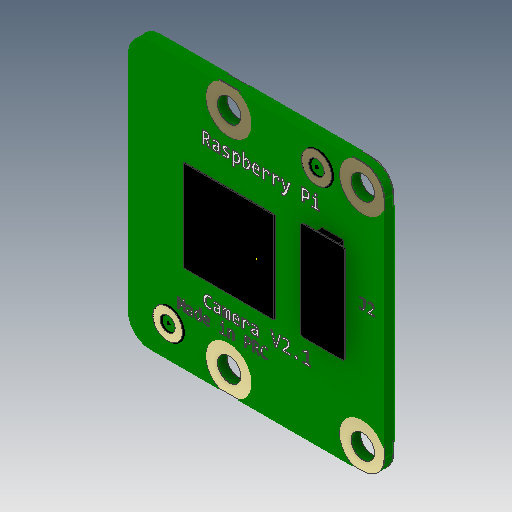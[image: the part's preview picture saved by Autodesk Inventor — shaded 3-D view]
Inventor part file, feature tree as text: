
AUTODESK INVENTOR PART (.ipt)
format: ipt  version: 2020 (Build 240168000, 168)  size: 2,342,912 bytes
history: native  units: mm
features: other x18, extrude x10, sketch x5, projected_geometry x5, hole x1, fillet x1
ambient origin geometry x8: Origin, YZ Plane, XZ Plane, XY Plane, X Axis, Y Axis, Z Axis, Center Point
bodies: Body1 (feature_tree), Body2 (feature_tree), Body3 (feature_tree), Body4 (feature_tree), Body5 (feature_tree), Body6 (feature_tree), Body7 (feature_tree), Body8 (feature_tree), Body9 (feature_tree)
feature tree (40):
  other  "PCB"
  sketch  "Boceto1"  dims[d0=23.862mm d1=25.0mm]
  extrude  "PCB_EXT"  Depth=25.0mm
  hole  "PADS_PCB_DRILL"  [1 undecoded]
  sketch  "Boceto2"  dims[d7=2.0mm d8=2.0mm]
  extrude  "PADS_PCB_DRILL_EXT"  Depth=1.0mm TaperAngle=0.0deg
  other  "FOTO"
  other  "SUPERIOR_PADS"
  extrude  "PADS_GOLDEN_UPPER_EXT"  Depth=2.2mm
  other  "INFERIOR_PADS"
  extrude  "PADS_GOLDEN_LOWER_EXT"  Depth=0.2mm
  extrude  "TEXTS_EXT"  Depth=0.2mm
  other  "REF_CON"
  extrude  "CONN"  Depth=0.2mm
  extrude  "CAM_BED"  Depth=0.2mm TaperAngle=0.0deg
  other  "PLANO_CON"
  extrude  "CONN_TOP"  Depth=0.2mm
  fillet  "Empalme2"  [1 undecoded]
  other  "REF_PADS_DRAW"
  extrude  "REF_PADS_DIAGONAL"  Depth=0.2mm TaperAngle=0.0deg
  extrude  "REF_PAD_BACK"  TaperAngle=90.0deg  [1 undecoded]
  other  "Imagen3"
  sketch  "Boceto4"  dims[d9=20.0mm d11=12.5mm d12=20.0mm d14=21.0mm d17=1.0mm d18=0.0mm]
  projected_geometry  "Contorno proyectado1"
  other  "PADS_UPPER"
  sketch  "Boceto5"  dims[d19=2.2mm d20=6.0mm d21=4.4mm d22=0.12mm d23=90.0deg d24=8.0mm d25=20.594885mm d26=2.0mm]
  projected_geometry  "Contorno proyectado2"
  projected_geometry  "Contorno proyectado3"
  projected_geometry  "Contorno proyectado4"
  projected_geometry  "Contorno proyectado5"
  other  "PADS_LOWER"
  other  "text_front"
  other  "TEXTS"
  other  "CAMERA_BED"
  sketch  "Boceto8"  dims[d27=4.4mm d28=4.4mm d29=4.4mm d30=4.4mm d31=0.13mm d32=0.0mm d57=24.8mm d63=90.0deg d66=0.07mm d67=0.0mm d68=90.0deg d69=0.07mm d70=0.0mm d71=0.03mm d72=0.0mm d74=8.5mm d75=8.5mm d78=5.212mm d79=8.25mm d82=4.7mm d86=2.2mm d87=8.5mm d88=0.5mm d89=1.0mm d90=0.0mm d91=0.1mm d92=0.0mm d93=90.0deg d94=0.1mm d95=0.0mm d97=0.2mm d98=13.8mm d101=0.1mm d102=0.0mm d115=0.1mm d116=0.0mm]
  other  "CONNECTOR"
  other  "PLACEMENT_CAM"
  other  "OUTSIDE_REF"
  other  "ref_pad_back_draw"
  other  "REF_PAD_BACK_PCB"
note: 3 required parameter values undecoded (feature->parameter linkage not recoverable at this tier; creation-order binding heuristic only, values carry confidence <= 0.55)
